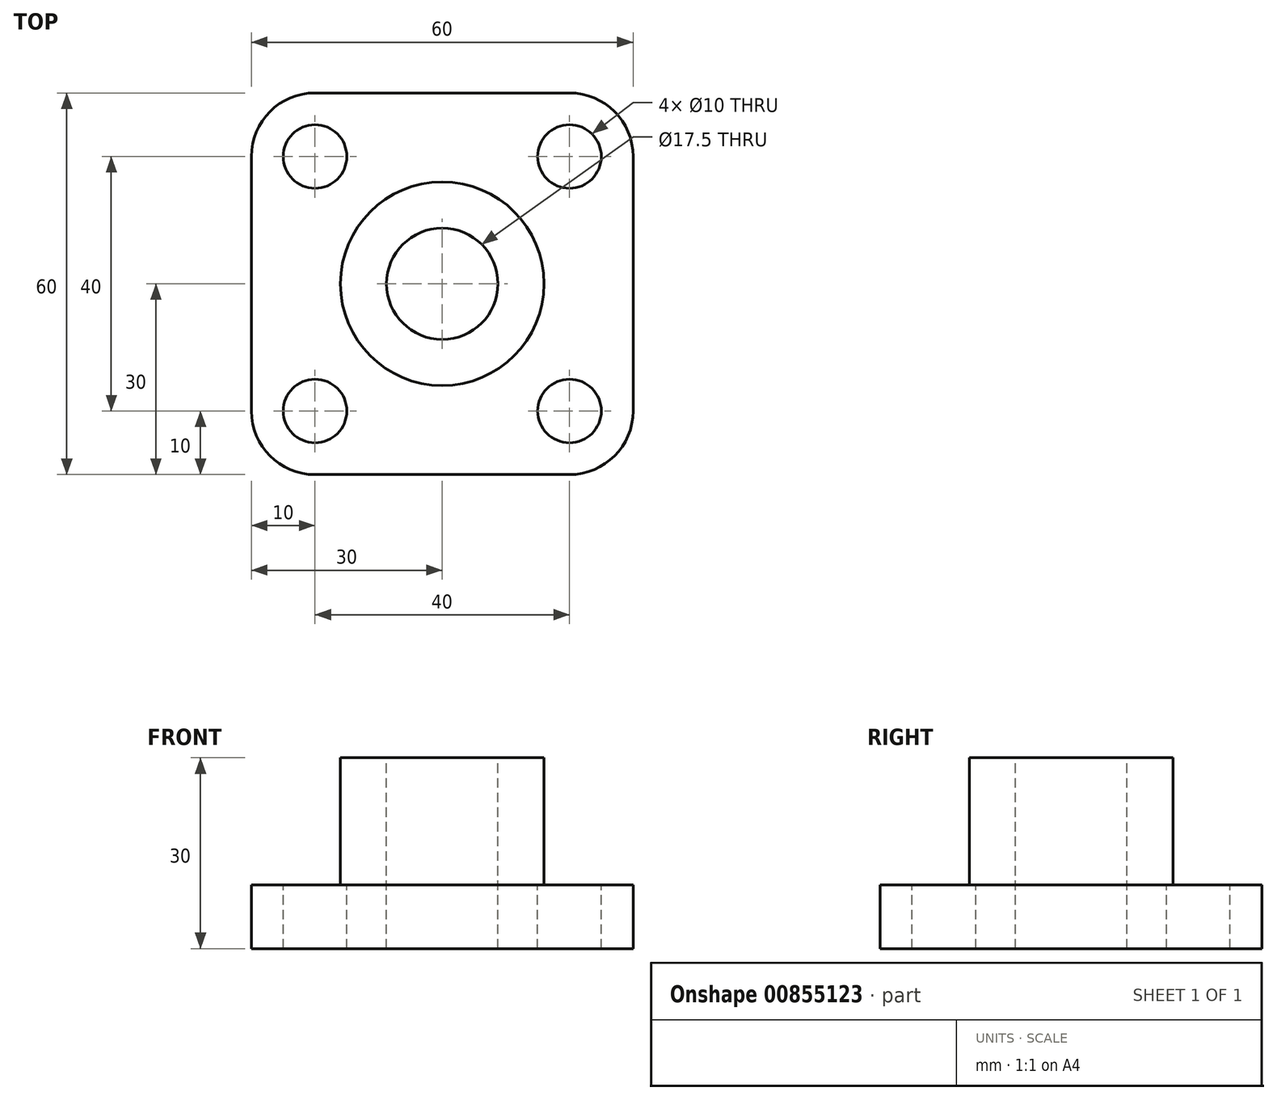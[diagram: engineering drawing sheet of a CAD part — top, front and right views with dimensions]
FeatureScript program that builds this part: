
annotation { "Feature Type Name" : "Feature", "Feature Type Description" : "" }
export const myFeature = defineFeature(function(context is Context, id is Id, definition is map)
    precondition{}
    {
        {
            var Q0;
            Q0=qCreatedBy(makeId("Top.planeOp"),FACE);
            var sketch = newSketch(context, id + "F0", { "sketchPlane" : qUnion([Q0])});
            skLineSegment(sketch, "E0.bottom", {"start": v(-20, 30) * mm, "end": v(20, 30) * mm});
            skLineSegment(sketch, "E0.top", {"start": v(-20, -30) * mm, "end": v(20, -30) * mm});
            skLineSegment(sketch, "E0.left", {"start": v(-30, 20) * mm, "end": v(-30, -20) * mm});
            skLineSegment(sketch, "E0.right", {"start": v(30, 20) * mm, "end": v(30, -20) * mm});
            skPoint(sketch, "E0.middle", {"position": v(0, 0) * mm});
            skArc(sketch, "E1.filletArc", {"start": v(-20, 30) * mm, "mid": v(-27.07, 27.07) * mm, "end": v(-30, 20) * mm});
            skArc(sketch, "E2.filletArc", {"start": v(30, 20) * mm, "mid": v(27.07, 27.07) * mm, "end": v(20, 30) * mm});
            skArc(sketch, "E3.filletArc", {"start": v(20, -30) * mm, "mid": v(27.07, -27.07) * mm, "end": v(30, -20) * mm});
            skArc(sketch, "E4.filletArc", {"start": v(-30, -20) * mm, "mid": v(-27.07, -27.07) * mm, "end": v(-20, -30) * mm});
            skCircle(sketch, "E5", {"center": v(-20, 20) * mm, "radius": 5 * mm});
            skCircle(sketch, "E6", {"center": v(20, 20) * mm, "radius": 5 * mm});
            skCircle(sketch, "E7", {"center": v(20, -20) * mm, "radius": 5 * mm});
            skCircle(sketch, "E8", {"center": v(-20, -20) * mm, "radius": 5 * mm});
            skCircle(sketch, "E9", {"center": v(0, 0) * mm, "radius": 16 * mm});
            skLineSegment(sketch, "E10", {"start": v(0, 0) * mm, "end": v(0, 48.19) * mm});
            skLineSegment(sketch, "E11", {"start": v(0, 0) * mm, "end": v(0, -48.88) * mm});
            skLineSegment(sketch, "E12", {"start": v(0, 0) * mm, "end": v(-39.95, 0) * mm});
            skLineSegment(sketch, "E13", {"start": v(0, 0) * mm, "end": v(39.95, 0) * mm});
            skSolve(sketch);
        }
        {
            var Q0;
            Q0 = qSketchRegion(id + "F0", true);
            var Q1;
            {var subQ0=sQuery(id+"F0.wireOp",EDGE,"E10");var subQ1=sQuery(id+"F0.wireOp",EDGE,"E9");var subQ2=makeQuery(id+"F0.imprint","INTERSECT",VERTEX,{"derivedFrom":[subQ1,subQ0]});Q1=makeQuery(id+"F0.imprint","IMPRINT",FACE,{"disambiguationData":[TD([[makeQuery(id+"F0.imprint","IMPRINT",EDGE,{"disambiguationData":[TD([[subQ2,-1.0]])],"derivedFrom":subQ1}),1.0]])]});}
            var Q2;
            {var subQ0=sQuery(id+"F0.wireOp",EDGE,"E10");var subQ1=sQuery(id+"F0.wireOp",EDGE,"E9");var subQ2=makeQuery(id+"F0.imprint","INTERSECT",VERTEX,{"derivedFrom":[subQ1,subQ0]});Q2=makeQuery(id+"F0.imprint","IMPRINT",FACE,{"disambiguationData":[TD([[makeQuery(id+"F0.imprint","IMPRINT",EDGE,{"disambiguationData":[TD([[subQ2,1.0]])],"derivedFrom":subQ1}),1.0]])]});}
            var Q3;
            {var subQ0=sQuery(id+"F0.wireOp",EDGE,"E13");var subQ1=sQuery(id+"F0.wireOp",EDGE,"E9");var subQ2=makeQuery(id+"F0.imprint","INTERSECT",VERTEX,{"derivedFrom":[subQ1,subQ0]});Q3=makeQuery(id+"F0.imprint","IMPRINT",FACE,{"disambiguationData":[TD([[makeQuery(id+"F0.imprint","IMPRINT",EDGE,{"disambiguationData":[TD([[subQ2,1.0]])],"derivedFrom":subQ1}),1.0]])]});}
            var Q4;
            Q4=makeQuery(id+"F0.imprint","IMPRINT",FACE,{"disambiguationData":[TD([[makeQuery(id+"F0.imprint","IMPRINT",EDGE,{"derivedFrom":sQuery(id+"F0.wireOp",EDGE,"E5")}),1.0]])]});
            var Q5;
            Q5=makeQuery(id+"F0.imprint","IMPRINT",FACE,{"disambiguationData":[TD([[makeQuery(id+"F0.imprint","IMPRINT",EDGE,{"derivedFrom":sQuery(id+"F0.wireOp",EDGE,"E6")}),1.0]])]});
            var Q6;
            {var subQ0=sQuery(id+"F0.wireOp",EDGE,"E12");var subQ1=sQuery(id+"F0.wireOp",EDGE,"E9");var subQ2=makeQuery(id+"F0.imprint","INTERSECT",VERTEX,{"derivedFrom":[subQ1,subQ0]});Q6=makeQuery(id+"F0.imprint","IMPRINT",FACE,{"disambiguationData":[TD([[makeQuery(id+"F0.imprint","IMPRINT",EDGE,{"disambiguationData":[TD([[subQ2,-1.0]])],"derivedFrom":subQ1}),1.0]])]});}
            var Q7;
            Q7=makeQuery(id+"F0.imprint","IMPRINT",FACE,{"disambiguationData":[TD([[makeQuery(id+"F0.imprint","IMPRINT",EDGE,{"derivedFrom":sQuery(id+"F0.wireOp",EDGE,"E7")}),1.0]])]});
            var Q8;
            Q8=makeQuery(id+"F0.imprint","IMPRINT",FACE,{"disambiguationData":[TD([[makeQuery(id+"F0.imprint","IMPRINT",EDGE,{"derivedFrom":sQuery(id+"F0.wireOp",EDGE,"E8")}),1.0]])]});
            extrude(context, id + "F1", {"entities" : qUnion([Q0, Q1, Q2, Q3, Q4, Q5, Q6, Q7, Q8]), "oppositeDirection" : true, "depth" : 10 * mm, "offsetDistance" : 25 * mm});
        }
        {
            var Q0;
            Q0=sQuery(id+"F0.wireOp",VERTEX,"E1.filletArc.center");
            var Q1;
            Q1=makeQuery(id+"F1.opExtrude","SWEPT_BODY",BODY,{"disambiguationData":[OSD([sQuery(id+"F0.wireOp",EDGE,"E0.bottom"),sQuery(id+"F0.wireOp",EDGE,"E0.top"),sQuery(id+"F0.wireOp",EDGE,"E0.left"),sQuery(id+"F0.wireOp",EDGE,"E0.right"),sQuery(id+"F0.wireOp",EDGE,"E1.filletArc"),sQuery(id+"F0.wireOp",EDGE,"E2.filletArc"),sQuery(id+"F0.wireOp",EDGE,"E3.filletArc"),sQuery(id+"F0.wireOp",EDGE,"E4.filletArc")])]});
            hole(context, id + "F2", {"style" : HoleStyle.SIMPLE, "endStyle" : HoleEndStyle.THROUGH, "holeDiameter" : 10 * mm, "majorDiameter" : 16 * mm, "isTappedThrough" : true, "tappedDepth" : 19 * mm, "tapClearance" : 3, "locations" : qUnion([Q0]), "scope" : qUnion([Q1])});
        }
        {
            var Q0;
            Q0=sQuery(id+"F0.wireOp",VERTEX,"E2.filletArc.center");
            var Q1;
            Q1=makeQuery(id+"F1.opExtrude","SWEPT_BODY",BODY,{"disambiguationData":[OSD([sQuery(id+"F0.wireOp",EDGE,"E0.bottom"),sQuery(id+"F0.wireOp",EDGE,"E0.top"),sQuery(id+"F0.wireOp",EDGE,"E0.left"),sQuery(id+"F0.wireOp",EDGE,"E0.right"),sQuery(id+"F0.wireOp",EDGE,"E1.filletArc"),sQuery(id+"F0.wireOp",EDGE,"E2.filletArc"),sQuery(id+"F0.wireOp",EDGE,"E3.filletArc"),sQuery(id+"F0.wireOp",EDGE,"E4.filletArc")])]});
            hole(context, id + "F3", {"style" : HoleStyle.SIMPLE, "endStyle" : HoleEndStyle.THROUGH, "holeDiameter" : 10 * mm, "majorDiameter" : 5 * mm, "isTappedThrough" : true, "tappedDepth" : 19 * mm, "tapClearance" : 3, "locations" : qUnion([Q0]), "scope" : qUnion([Q1])});
        }
        {
            var Q0;
            Q0=sQuery(id+"F0.wireOp",VERTEX,"E3.filletArc.center");
            var Q1;
            Q1=makeQuery(id+"F1.opExtrude","SWEPT_BODY",BODY,{"disambiguationData":[OSD([sQuery(id+"F0.wireOp",EDGE,"E0.bottom"),sQuery(id+"F0.wireOp",EDGE,"E0.top"),sQuery(id+"F0.wireOp",EDGE,"E0.left"),sQuery(id+"F0.wireOp",EDGE,"E0.right"),sQuery(id+"F0.wireOp",EDGE,"E1.filletArc"),sQuery(id+"F0.wireOp",EDGE,"E2.filletArc"),sQuery(id+"F0.wireOp",EDGE,"E3.filletArc"),sQuery(id+"F0.wireOp",EDGE,"E4.filletArc")])]});
            hole(context, id + "F4", {"style" : HoleStyle.SIMPLE, "endStyle" : HoleEndStyle.THROUGH, "holeDiameter" : 10 * mm, "majorDiameter" : 5 * mm, "isTappedThrough" : true, "tappedDepth" : 19 * mm, "tapClearance" : 3, "locations" : qUnion([Q0]), "scope" : qUnion([Q1])});
        }
        {
            var Q0;
            Q0=sQuery(id+"F0.wireOp",VERTEX,"E4.filletArc.center");
            var Q1;
            Q1=makeQuery(id+"F1.opExtrude","SWEPT_BODY",BODY,{"disambiguationData":[OSD([sQuery(id+"F0.wireOp",EDGE,"E0.bottom"),sQuery(id+"F0.wireOp",EDGE,"E0.top"),sQuery(id+"F0.wireOp",EDGE,"E0.left"),sQuery(id+"F0.wireOp",EDGE,"E0.right"),sQuery(id+"F0.wireOp",EDGE,"E1.filletArc"),sQuery(id+"F0.wireOp",EDGE,"E2.filletArc"),sQuery(id+"F0.wireOp",EDGE,"E3.filletArc"),sQuery(id+"F0.wireOp",EDGE,"E4.filletArc")])]});
            hole(context, id + "F5", {"style" : HoleStyle.SIMPLE, "endStyle" : HoleEndStyle.THROUGH, "holeDiameter" : 10 * mm, "majorDiameter" : 5 * mm, "isTappedThrough" : true, "tappedDepth" : 19 * mm, "tapClearance" : 3, "locations" : qUnion([Q0]), "scope" : qUnion([Q1])});
        }
        {
            var Q0;
            {var subQ0=sQuery(id+"F0.wireOp",EDGE,"a0VSIp49-t4PJ-wajc-gBmh-iXeknJD0HQHf");Q0=makeQuery(id+"F0.imprint","IMPRINT",FACE,{"disambiguationData":[TD([[makeQuery(id+"F0.imprint","IMPRINT",EDGE,{"derivedFrom":subQ0}),-1.0]])]});}
            var Q1;
            {var subQ0=sQuery(id+"F0.wireOp",EDGE,"9XHfqxow-xhiB-PsX0-32QW-jo9Z5O20xCbV");Q1=makeQuery(id+"F0.imprint","IMPRINT",FACE,{"disambiguationData":[TD([[makeQuery(id+"F0.imprint","IMPRINT",EDGE,{"derivedFrom":subQ0}),1.0]])]});}
            var Q2;
            {var subQ0=sQuery(id+"F0.wireOp",EDGE,"P2uUQQQb-GWus-Cm4R-ULZp-TCOrGr6IWHym");Q2=makeQuery(id+"F0.imprint","IMPRINT",FACE,{"disambiguationData":[TD([[makeQuery(id+"F0.imprint","IMPRINT",EDGE,{"derivedFrom":subQ0}),-1.0]])]});}
            var Q3;
            {var subQ0=sQuery(id+"F0.wireOp",EDGE,"OOL3tmgB-M9TP-O1MH-f3bP-JQHe8RYlHLSN");Q3=makeQuery(id+"F0.imprint","IMPRINT",FACE,{"disambiguationData":[TD([[makeQuery(id+"F0.imprint","IMPRINT",EDGE,{"derivedFrom":subQ0}),1.0]])]});}
            var Q4;
            {var subQ0=sQuery(id+"F0.wireOp",EDGE,"PUbJ4SlO-Ba4Y-cCN3-dyeq-0uOaFZrOorBd");Q4=makeQuery(id+"F0.imprint","IMPRINT",FACE,{"disambiguationData":[TD([[makeQuery(id+"F0.imprint","IMPRINT",EDGE,{"derivedFrom":subQ0}),-1.0]])]});}
            var Q5;
            {var subQ0=sQuery(id+"F0.wireOp",EDGE,"u7Rc682n-bvA8-MZBG-F1Hz-DrzD7w1FtVKo");Q5=makeQuery(id+"F0.imprint","IMPRINT",FACE,{"disambiguationData":[TD([[makeQuery(id+"F0.imprint","IMPRINT",EDGE,{"derivedFrom":subQ0}),1.0]])]});}
            var Q6;
            {var subQ0=sQuery(id+"F0.wireOp",EDGE,"XrzCbF5e-DQrz-hXQY-LDlF-oldrlcenxuC6");Q6=makeQuery(id+"F0.imprint","IMPRINT",FACE,{"disambiguationData":[TD([[makeQuery(id+"F0.imprint","IMPRINT",EDGE,{"derivedFrom":subQ0}),1.0]])]});}
            var Q7;
            {var subQ0=sQuery(id+"F0.wireOp",EDGE,"To3jkKhw-Gv3E-OCU6-TJrY-gAZLhhwv7KjD");Q7=makeQuery(id+"F0.imprint","IMPRINT",FACE,{"disambiguationData":[TD([[makeQuery(id+"F0.imprint","IMPRINT",EDGE,{"derivedFrom":subQ0}),-1.0]])]});}
            var Q8;
            {var subQ3=sQuery(id+"F0.wireOp",EDGE,"E9");var subQ6=makeQuery(id+"F0.imprint","INTERSECT",VERTEX,{"derivedFrom":[subQ3,sQuery(id+"F0.wireOp",EDGE,"9XHfqxow-xhiB-PsX0-32QW-jo9Z5O20xCbV")]});Q8=makeQuery(id+"F0.imprint","IMPRINT",FACE,{"disambiguationData":[TD([[makeQuery(id+"F0.imprint","IMPRINT",EDGE,{"disambiguationData":[TD([[subQ6,1.0]])],"derivedFrom":subQ3}),1.0]])]});}
            var Q9;
            {var subQ0=sQuery(id+"F0.wireOp",EDGE,"E9");var subQ4=makeQuery(id+"F0.imprint","INTERSECT",VERTEX,{"derivedFrom":[subQ0,sQuery(id+"F0.wireOp",EDGE,"XrzCbF5e-DQrz-hXQY-LDlF-oldrlcenxuC6")]});Q9=makeQuery(id+"F0.imprint","IMPRINT",FACE,{"disambiguationData":[TD([[makeQuery(id+"F0.imprint","IMPRINT",EDGE,{"disambiguationData":[TD([[subQ4,1.0]])],"derivedFrom":subQ0}),1.0]])]});}
            var Q10;
            {var subQ3=sQuery(id+"F0.wireOp",EDGE,"E9");var subQ6=makeQuery(id+"F0.imprint","INTERSECT",VERTEX,{"derivedFrom":[subQ3,sQuery(id+"F0.wireOp",EDGE,"OOL3tmgB-M9TP-O1MH-f3bP-JQHe8RYlHLSN")]});Q10=makeQuery(id+"F0.imprint","IMPRINT",FACE,{"disambiguationData":[TD([[makeQuery(id+"F0.imprint","IMPRINT",EDGE,{"disambiguationData":[TD([[subQ6,1.0]])],"derivedFrom":subQ3}),1.0]])]});}
            var Q11;
            {var subQ3=sQuery(id+"F0.wireOp",EDGE,"E9");var subQ7=makeQuery(id+"F0.imprint","INTERSECT",VERTEX,{"derivedFrom":[subQ3,sQuery(id+"F0.wireOp",EDGE,"u7Rc682n-bvA8-MZBG-F1Hz-DrzD7w1FtVKo")]});Q11=makeQuery(id+"F0.imprint","IMPRINT",FACE,{"disambiguationData":[TD([[makeQuery(id+"F0.imprint","IMPRINT",EDGE,{"disambiguationData":[TD([[subQ7,1.0]])],"derivedFrom":subQ3}),1.0]])]});}
            extrude(context, id + "F6", {"entities" : qUnion([Q0, Q1, Q2, Q3, Q4, Q5, Q6, Q7, Q8, Q9, Q10, Q11]), "operationType" : NewBodyOperationType.ADD, "depth" : 20 * mm, "offsetDistance" : 25 * mm});
        }
        {
            var Q0;
            Q0=makeQuery(id+"F6.opExtrude","CAP_FACE",FACE,{"disambiguationData":[OSD([sQuery(id+"F0.wireOp",EDGE,"E9"),sQuery(id+"F0.wireOp",EDGE,"71ufA5jk-GuGM-Vrxq-4NkH-q18k1E7h9voU"),sQuery(id+"F0.wireOp",EDGE,"XrzCbF5e-DQrz-hXQY-LDlF-oldrlcenxuC6"),sQuery(id+"F0.wireOp",EDGE,"To3jkKhw-Gv3E-OCU6-TJrY-gAZLhhwv7KjD"),sQuery(id+"F0.wireOp",EDGE,"0iUhdisK-JLgk-rzHg-Ur0L-2ECTcfuGwbMc"),sQuery(id+"F0.wireOp",EDGE,"9XHfqxow-xhiB-PsX0-32QW-jo9Z5O20xCbV"),sQuery(id+"F0.wireOp",EDGE,"a0VSIp49-t4PJ-wajc-gBmh-iXeknJD0HQHf"),sQuery(id+"F0.wireOp",EDGE,"0kztOIQi-QDeY-rdza-lKLz-d534mFDWz6QF"),sQuery(id+"F0.wireOp",EDGE,"PUbJ4SlO-Ba4Y-cCN3-dyeq-0uOaFZrOorBd"),sQuery(id+"F0.wireOp",EDGE,"u7Rc682n-bvA8-MZBG-F1Hz-DrzD7w1FtVKo"),sQuery(id+"F0.wireOp",EDGE,"P2uUQQQb-GWus-Cm4R-ULZp-TCOrGr6IWHym"),sQuery(id+"F0.wireOp",EDGE,"9Hsa5OiI-STgt-fhpu-GyKi-megqv78sB2Rf"),sQuery(id+"F0.wireOp",EDGE,"OOL3tmgB-M9TP-O1MH-f3bP-JQHe8RYlHLSN")])],"isStart":false});
            var sketch = newSketch(context, id + "F7", { "sketchPlane" : qUnion([Q0])});
            skPoint(sketch, "E14", {"position": v(0, 0) * mm});
            skLineSegment(sketch, "E15", {"start": v(0, 0) * mm, "end": v(0, -47.48) * mm});
            skLineSegment(sketch, "E16", {"start": v(0, 0) * mm, "end": v(0, 56.34) * mm});
            skLineSegment(sketch, "E17", {"start": v(0, 0) * mm, "end": v(-35.65, 0) * mm});
            skLineSegment(sketch, "E18", {"start": v(0, 0) * mm, "end": v(47.08, 0) * mm});
            skSolve(sketch);
        }
        {
            var Q0;
            Q0=sQuery(id+"F7.wireOp",VERTEX,"E15.start");
            var Q1;
            Q1=makeQuery(id+"F1.opExtrude","SWEPT_BODY",BODY,{"disambiguationData":[OSD([sQuery(id+"F0.wireOp",EDGE,"E0.bottom"),sQuery(id+"F0.wireOp",EDGE,"E0.top"),sQuery(id+"F0.wireOp",EDGE,"E0.left"),sQuery(id+"F0.wireOp",EDGE,"E0.right"),sQuery(id+"F0.wireOp",EDGE,"E1.filletArc"),sQuery(id+"F0.wireOp",EDGE,"E2.filletArc"),sQuery(id+"F0.wireOp",EDGE,"E3.filletArc"),sQuery(id+"F0.wireOp",EDGE,"E4.filletArc"),sQuery(id+"F0.wireOp",EDGE,"71ufA5jk-GuGM-Vrxq-4NkH-q18k1E7h9voU"),sQuery(id+"F0.wireOp",EDGE,"0iUhdisK-JLgk-rzHg-Ur0L-2ECTcfuGwbMc"),sQuery(id+"F0.wireOp",EDGE,"0kztOIQi-QDeY-rdza-lKLz-d534mFDWz6QF"),sQuery(id+"F0.wireOp",EDGE,"9Hsa5OiI-STgt-fhpu-GyKi-megqv78sB2Rf")])]});
            hole(context, id + "F8", {"style" : HoleStyle.SIMPLE, "endStyle" : HoleEndStyle.THROUGH, "standardTappedOrClearance" : lookupTablePath({ "fit" : "Normal", "standard" : "ISO", "size" : "M16", "type" : "Clearance" }), "standardBlindInLast" : lookupTablePath({ "fit" : "Standard", "standard" : "ISO", "size" : "M16", "type" : "Clearance" }), "holeDiameter" : 17.5 * mm, "majorDiameter" : 5 * mm, "isTappedThrough" : true, "tappedDepth" : 19 * mm, "tapClearance" : 3, "locations" : qUnion([Q0]), "scope" : qUnion([Q1])});
        }
    });
